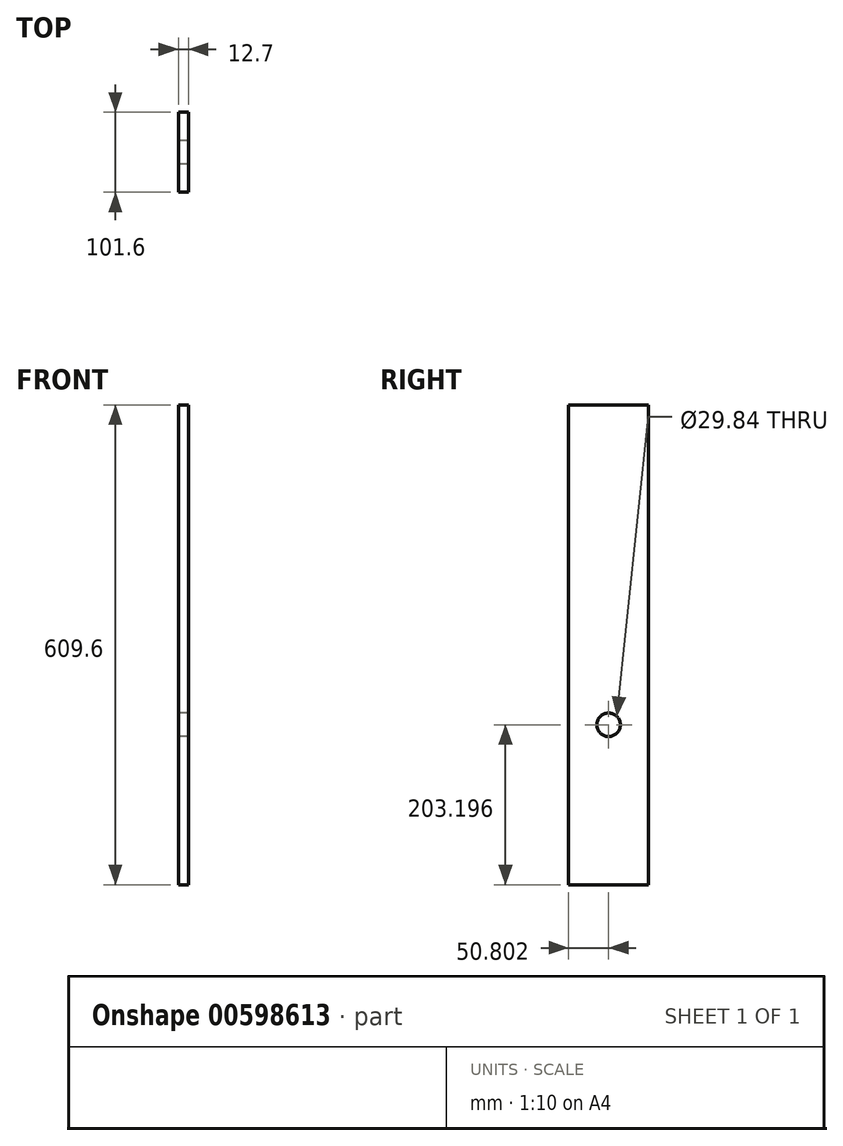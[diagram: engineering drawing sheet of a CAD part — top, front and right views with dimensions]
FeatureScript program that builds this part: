
annotation { "Feature Type Name" : "Feature", "Feature Type Description" : "" }
export const myFeature = defineFeature(function(context is Context, id is Id, definition is map)
    precondition{}
    {
        {
            var Q0;
            Q0=qCreatedBy(makeId("Right.planeOp"),FACE);
            var sketch = newSketch(context, id + "F0", { "sketchPlane" : qUnion([Q0])});
            skLineSegment(sketch, "E0.bottom", {"start": v(-56.38, 298.32) * mm, "end": v(45.22, 298.32) * mm});
            skLineSegment(sketch, "E0.top", {"start": v(-56.38, -311.28) * mm, "end": v(45.22, -311.28) * mm});
            skLineSegment(sketch, "E0.left", {"start": v(-56.38, 298.32) * mm, "end": v(-56.38, -311.28) * mm});
            skLineSegment(sketch, "E0.right", {"start": v(45.22, 298.32) * mm, "end": v(45.22, -311.28) * mm});
            skLineSegment(sketch, "E1", {"start": v(-5.58, -311.28) * mm, "end": v(-5.58, -108.08) * mm, "construction": true});
            skCircle(sketch, "E2", {"center": v(-5.58, -108.08) * mm, "radius": 14.92 * mm});
            skSolve(sketch);
        }
        {
            var Q0;
            Q0=makeQuery(id+"F0.imprint","IMPRINT",FACE,{"disambiguationData":[TD([[makeQuery(id+"F0.imprint","IMPRINT",EDGE,{"derivedFrom":sQuery(id+"F0.wireOp",EDGE,"E0.bottom")}),-1.0]])]});
            extrude(context, id + "F1", {"entities" : qUnion([Q0]), "depth" : 12.7 * mm, "offsetDistance" : 25.4 * mm});
        }
        {
            var Q0;
            Q0 = qSketchRegion(id + "F0", true);
            extrude(context, id + "F2", {"entities" : qUnion([Q0]), "operationType" : NewBodyOperationType.ADD, "depth" : 12.7 * mm, "offsetDistance" : 25.4 * mm});
        }
    });
